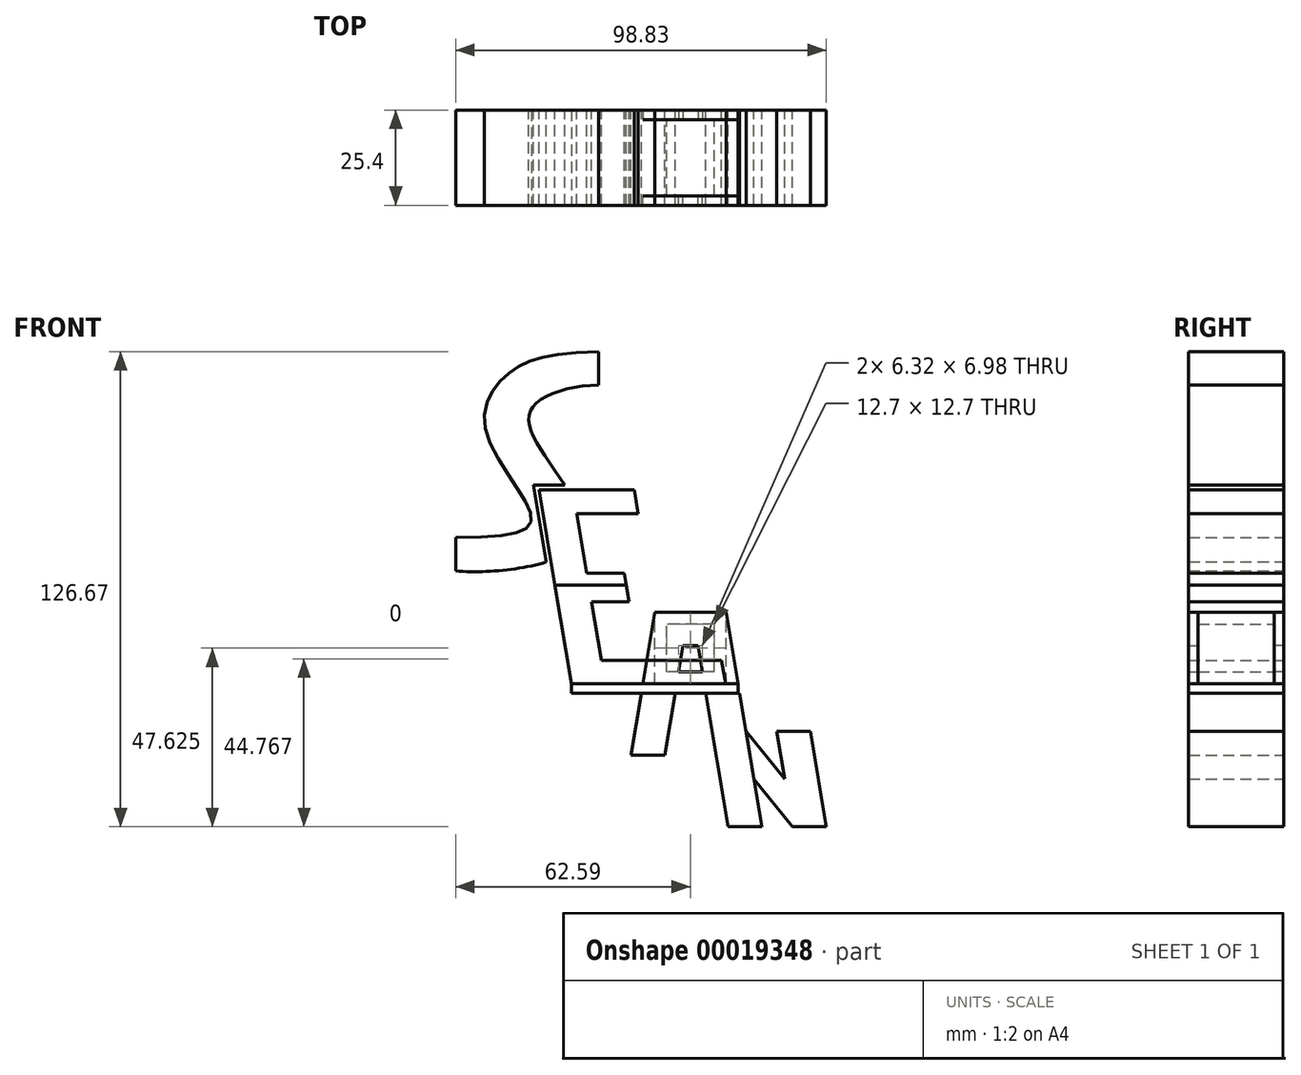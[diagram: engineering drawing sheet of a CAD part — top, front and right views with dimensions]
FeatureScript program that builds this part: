
annotation { "Feature Type Name" : "Feature", "Feature Type Description" : "" }
export const myFeature = defineFeature(function(context is Context, id is Id, definition is map)
    precondition{}
    {
        {
            var Q0;
            Q0=qCreatedBy(makeId("Top.planeOp"),FACE);
            var sketch = newSketch(context, id + "F0", { "sketchPlane" : qUnion([Q0])});
            skLineSegment(sketch, "E0.bottom", {"start": v(-44.45, 12.7) * mm, "end": v(0, 12.7) * mm});
            skLineSegment(sketch, "E0.top", {"start": v(-44.45, -12.7) * mm, "end": v(0, -12.7) * mm});
            skLineSegment(sketch, "E0.left", {"start": v(-44.45, 12.7) * mm, "end": v(-44.45, -12.7) * mm});
            skLineSegment(sketch, "E0.right", {"start": v(0, 12.7) * mm, "end": v(0, -12.7) * mm});
            skSolve(sketch);
        }
        {
            var Q0;
            Q0=makeQuery(id+"F0.imprint","IMPRINT",FACE,{"disambiguationData":[TD([[makeQuery(id+"F0.imprint","IMPRINT",EDGE,{"derivedFrom":sQuery(id+"F0.wireOp",EDGE,"E0.bottom")}),-1.0]])]});
            extrude(context, id + "F1", {"entities" : qUnion([Q0]), "depth" : 2.54 * mm});
        }
        {
            var Q0;
            Q0=qCreatedBy(makeId("Front.planeOp"),FACE);
            var sketch = newSketch(context, id + "F2", { "sketchPlane" : qUnion([Q0])});
            skPoint(sketch, "E1.0", {"position": v(0, 2.54) * mm});
            skLineSegment(sketch, "E2.bottom", {"start": v(-3.18, 2.54) * mm, "end": v(-22.22, 2.54) * mm});
            skLineSegment(sketch, "E2.top", {"start": v(-3.18, 21.6) * mm, "end": v(-22.22, 21.6) * mm});
            skLineSegment(sketch, "E2.left", {"start": v(-3.18, 2.54) * mm, "end": v(-3.18, 21.6) * mm});
            skLineSegment(sketch, "E2.right", {"start": v(-22.22, 2.54) * mm, "end": v(-22.22, 21.6) * mm});
            skLineSegment(sketch, "E3.0", {"start": v(-19.05, 5.72) * mm, "end": v(-19.05, 18.42) * mm});
            skLineSegment(sketch, "E3.1", {"start": v(-6.35, 5.72) * mm, "end": v(-19.05, 5.72) * mm});
            skLineSegment(sketch, "E3.2", {"start": v(-6.35, 5.72) * mm, "end": v(-6.35, 18.42) * mm});
            skLineSegment(sketch, "E3.3", {"start": v(-6.35, 18.42) * mm, "end": v(-19.05, 18.42) * mm});
            skSolve(sketch);
        }
        {
            var Q0;
            Q0=makeQuery(id+"F2.imprint","IMPRINT",FACE,{"disambiguationData":[TD([[makeQuery(id+"F2.imprint","IMPRINT",EDGE,{"derivedFrom":sQuery(id+"F2.wireOp",EDGE,"E2.bottom")}),-1.0]])]});
            extrude(context, id + "F3", {"entities" : qUnion([Q0]), "endBound" : BoundingType.SYMMETRIC, "depth" : 20.32 * mm});
        }
        {
            var Q0;
            Q0=makeQuery(id+"F3.opExtrude","CAP_FACE",FACE,{"disambiguationData":[OSD([sQuery(id+"F2.wireOp",EDGE,"E2.bottom"),sQuery(id+"F2.wireOp",EDGE,"E2.top"),sQuery(id+"F2.wireOp",EDGE,"E2.left"),sQuery(id+"F2.wireOp",EDGE,"E2.right"),sQuery(id+"F2.wireOp",EDGE,"E3.0"),sQuery(id+"F2.wireOp",EDGE,"E3.1"),sQuery(id+"F2.wireOp",EDGE,"E3.2"),sQuery(id+"F2.wireOp",EDGE,"E3.3")])],"isStart":false});
            var sketch = newSketch(context, id + "F4", { "sketchPlane" : qUnion([Q0])});
            skPoint(sketch, "E4.0", {"position": v(0, 2.54) * mm});
            skLineSegment(sketch, "E5", {"start": v(0, 2.54) * mm, "end": v(-3.18, 21.6) * mm});
            skLineSegment(sketch, "E6", {"start": v(-3.18, 21.6) * mm, "end": v(-22.22, 21.6) * mm});
            skLineSegment(sketch, "E7", {"start": v(-22.22, 21.6) * mm, "end": v(-25.4, 2.54) * mm});
            skLineSegment(sketch, "E8", {"start": v(-25.4, 2.54) * mm, "end": v(0, 2.54) * mm});
            skLineSegment(sketch, "E9.0", {"start": v(-14.7, 12.7) * mm, "end": v(-15.86, 5.72) * mm});
            skLineSegment(sketch, "E9.1", {"start": v(-10.7, 12.7) * mm, "end": v(-14.7, 12.7) * mm});
            skLineSegment(sketch, "E9.2", {"start": v(-9.54, 5.72) * mm, "end": v(-10.7, 12.7) * mm});
            skLineSegment(sketch, "E9.3", {"start": v(-15.86, 5.72) * mm, "end": v(-9.54, 5.72) * mm});
            skLineSegment(sketch, "E10.0", {"start": v(-9.54, 5.72) * mm, "end": v(-15.86, 5.72) * mm});
            skPoint(sketch, "E11.orphan", {"position": v(-19.05, 5.72) * mm});
            skPoint(sketch, "E12.orphan", {"position": v(-6.35, 5.72) * mm});
            skSolve(sketch);
        }
        {
            var Q0;
            Q0 = qSketchRegion(id + "F4", true);
            var Q1;
            Q1=makeQuery(id+"F1.opExtrude","SWEPT_FACE",FACE,{"disambiguationData":[OSD([sQuery(id+"F0.wireOp",EDGE,"E0.top")])]});
            var Q2;
            Q2=makeQuery(id+"F1.opExtrude","SWEPT_BODY",BODY,{"disambiguationData":[OSD([sQuery(id+"F0.wireOp",EDGE,"E0.bottom"),sQuery(id+"F0.wireOp",EDGE,"E0.top"),sQuery(id+"F0.wireOp",EDGE,"E0.left"),sQuery(id+"F0.wireOp",EDGE,"E0.right")])]});
            extrude(context, id + "F5", {"entities" : qUnion([Q0]), "endBound" : BoundingType.UP_TO_SURFACE, "endBoundEntityFace" : qUnion([Q1]), "endBoundEntityBody" : qUnion([Q2]), "depth" : 25.4 * mm});
        }
        {
            var Q0;
            Q0=makeQuery(id+"F5.opExtrude","SWEPT_BODY",BODY,{"disambiguationData":[OSD([sQuery(id+"F4.wireOp",EDGE,"E5"),sQuery(id+"F4.wireOp",EDGE,"E6"),sQuery(id+"F4.wireOp",EDGE,"E7"),sQuery(id+"F4.wireOp",EDGE,"E8"),sQuery(id+"F4.wireOp",EDGE,"E9.0"),sQuery(id+"F4.wireOp",EDGE,"E9.1"),sQuery(id+"F4.wireOp",EDGE,"E9.2"),sQuery(id+"F4.wireOp",EDGE,"E10.0")])]});
            var Q1;
            Q1=qCreatedBy(makeId("Front.planeOp"),FACE);
            mirror(context, id + "F6", {"entities" : qUnion([Q0]), "mirrorPlane" : qUnion([Q1])});
        }
        {
            var Q0;
            Q0=qCreatedBy(makeId("Front.planeOp"),FACE);
            var sketch = newSketch(context, id + "F7", { "sketchPlane" : qUnion([Q0])});
            skPoint(sketch, "E13.0", {"position": v(-44.45, 2.54) * mm});
            skLineSegment(sketch, "E14", {"start": v(-44.45, 2.54) * mm, "end": v(-3.34, 2.54) * mm});
            skPoint(sketch, "E15.0", {"position": v(-22.22, 21.6) * mm});
            skLineSegment(sketch, "E16", {"start": v(-44.45, 2.54) * mm, "end": v(-48.83, 28.85) * mm});
            skLineSegment(sketch, "E17", {"start": v(-48.83, 28.85) * mm, "end": v(-29.78, 28.85) * mm});
            skLineSegment(sketch, "E18.0", {"start": v(-39.1, 24.46) * mm, "end": v(-29.05, 24.46) * mm});
            skLineSegment(sketch, "E18.1", {"start": v(-36.48, 8.8) * mm, "end": v(-39.1, 24.46) * mm});
            skLineSegment(sketch, "E18.2", {"start": v(-36.48, 8.8) * mm, "end": v(-4.38, 8.8) * mm});
            skLineSegment(sketch, "E19", {"start": v(-29.78, 28.85) * mm, "end": v(-29.05, 24.46) * mm});
            skLineSegment(sketch, "E20", {"start": v(-4.38, 8.8) * mm, "end": v(-3.34, 2.54) * mm});
            skSolve(sketch);
        }
        {
            var Q0;
            Q0=makeQuery(id+"F7.imprint","IMPRINT",FACE,{"disambiguationData":[TD([[makeQuery(id+"F7.imprint","IMPRINT",EDGE,{"derivedFrom":sQuery(id+"F7.wireOp",EDGE,"E14")}),1.0]])]});
            extrude(context, id + "F8", {"entities" : qUnion([Q0]), "endBound" : BoundingType.SYMMETRIC, "depth" : 25.4 * mm});
        }
        {
            var Q0;
            Q0=qCreatedBy(makeId("Front.planeOp"),FACE);
            var sketch = newSketch(context, id + "F9", { "sketchPlane" : qUnion([Q0])});
            skPoint(sketch, "E21.0", {"position": v(-48.83, 28.85) * mm});
            skPoint(sketch, "E22.0", {"position": v(-29.78, 28.85) * mm});
            skLineSegment(sketch, "E23", {"start": v(-48.83, 28.85) * mm, "end": v(-29.78, 28.85) * mm});
            skLineSegment(sketch, "E24", {"start": v(-48.83, 28.85) * mm, "end": v(-53.07, 54.25) * mm});
            skLineSegment(sketch, "E25", {"start": v(-53.07, 54.25) * mm, "end": v(-27.67, 54.25) * mm});
            skLineSegment(sketch, "E26.0", {"start": v(-43, 47.9) * mm, "end": v(-26.6, 47.9) * mm});
            skLineSegment(sketch, "E26.1", {"start": v(-40.34, 31.98) * mm, "end": v(-43, 47.9) * mm});
            skLineSegment(sketch, "E26.2", {"start": v(-40.34, 31.98) * mm, "end": v(-30.3, 31.98) * mm});
            skLineSegment(sketch, "E27", {"start": v(-27.67, 54.25) * mm, "end": v(-26.6, 47.9) * mm});
            skLineSegment(sketch, "E28", {"start": v(-30.3, 31.98) * mm, "end": v(-29.78, 28.85) * mm});
            skSolve(sketch);
        }
        {
            var Q0;
            Q0 = qSketchRegion(id + "F9", true);
            extrude(context, id + "F10", {"entities" : qUnion([Q0]), "endBound" : BoundingType.SYMMETRIC, "depth" : 25.4 * mm});
        }
        {
            var Q0;
            Q0=qCreatedBy(makeId("Front.planeOp"),FACE);
            var sketch = newSketch(context, id + "F11", { "sketchPlane" : qUnion([Q0])});
            skLineSegment(sketch, "E29.0", {"start": v(-25.4, 2.54) * mm, "end": v(-22.22, 21.6) * mm});
            skLineSegment(sketch, "E29.1", {"start": v(-14.7, 12.7) * mm, "end": v(-14.7, 12.7) * mm});
            skLineSegment(sketch, "E29.2", {"start": v(-10.7, 12.7) * mm, "end": v(-10.7, 12.7) * mm});
            skLineSegment(sketch, "E29.3", {"start": v(-3.18, 21.6) * mm, "end": v(0, 2.54) * mm});
            skLineSegment(sketch, "E30", {"start": v(-25.82, 0) * mm, "end": v(-28.58, -16.5) * mm});
            skLineSegment(sketch, "E31", {"start": v(-16.81, 0) * mm, "end": v(-19.56, -16.5) * mm});
            skLineSegment(sketch, "E32", {"start": v(-19.56, -16.5) * mm, "end": v(-28.58, -16.51) * mm});
            skLineSegment(sketch, "E33", {"start": v(-8.59, 0) * mm, "end": v(-2.66, -35.56) * mm});
            skLineSegment(sketch, "E34", {"start": v(0.42, 0) * mm, "end": v(6.35, -35.56) * mm});
            skLineSegment(sketch, "E35", {"start": v(6.35, -35.56) * mm, "end": v(-2.66, -35.56) * mm});
            skLineSegment(sketch, "E36.0", {"start": v(-25.82, 0) * mm, "end": v(-16.81, 0) * mm});
            skPoint(sketch, "E37.orphan", {"position": v(-44.45, 0) * mm});
            skLineSegment(sketch, "E38.trimOffspring", {"start": v(-8.59, 0) * mm, "end": v(0, 0) * mm});
            skLineSegment(sketch, "E39", {"start": v(0, 0) * mm, "end": v(0.42, 0) * mm});
            skSolve(sketch);
        }
        {
            var Q0;
            Q0=makeQuery(id+"F11.imprint","IMPRINT",FACE,{"disambiguationData":[TD([[makeQuery(id+"F11.imprint","IMPRINT",EDGE,{"derivedFrom":sQuery(id+"F11.wireOp",EDGE,"E30")}),1.0]])]});
            var Q1;
            Q1=makeQuery(id+"F11.imprint","IMPRINT",FACE,{"disambiguationData":[TD([[makeQuery(id+"F11.imprint","IMPRINT",EDGE,{"derivedFrom":sQuery(id+"F11.wireOp",EDGE,"E33")}),1.0]])]});
            extrude(context, id + "F12", {"entities" : qUnion([Q0, Q1]), "endBound" : BoundingType.SYMMETRIC, "depth" : 25.4 * mm});
        }
        {
            var Q0;
            Q0=qCreatedBy(makeId("Front.planeOp"),FACE);
            var sketch = newSketch(context, id + "F13", { "sketchPlane" : qUnion([Q0])});
            skPoint(sketch, "E40.0", {"position": v(-19.56, -16.5) * mm});
            skLineSegment(sketch, "E41.0", {"start": v(0.42, 0) * mm, "end": v(6.35, -35.56) * mm});
            skLineSegment(sketch, "E42", {"start": v(2.12, -10.16) * mm, "end": v(12.4, -22.86) * mm});
            skLineSegment(sketch, "E43", {"start": v(12.4, -22.86) * mm, "end": v(10.29, -10.16) * mm});
            skLineSegment(sketch, "E44", {"start": v(10.29, -10.16) * mm, "end": v(19.3, -10.16) * mm});
            skLineSegment(sketch, "E45", {"start": v(19.3, -10.16) * mm, "end": v(23.54, -35.56) * mm});
            skLineSegment(sketch, "E46", {"start": v(23.54, -35.56) * mm, "end": v(14.52, -35.56) * mm});
            skLineSegment(sketch, "E47", {"start": v(14.52, -35.56) * mm, "end": v(4.23, -22.86) * mm});
            skSolve(sketch);
        }
        {
            var Q0;
            {var subQ1=sQuery(id+"F13.wireOp",EDGE,"E42");Q0=makeQuery(id+"F13.imprint","IMPRINT",FACE,{"disambiguationData":[TD([[makeQuery(id+"F13.imprint","IMPRINT",EDGE,{"derivedFrom":subQ1}),-1.0]])]});}
            extrude(context, id + "F14", {"entities" : qUnion([Q0]), "endBound" : BoundingType.SYMMETRIC, "depth" : 25.4 * mm});
        }
        {
            var Q0;
            Q0=qCreatedBy(makeId("Front.planeOp"),FACE);
            var sketch = newSketch(context, id + "F15", { "sketchPlane" : qUnion([Q0])});
            skFitSpline(sketch, "E48", {"points": [v(-75.3, 32.6) * mm, v(-41.98, 41.06) * mm, v(-51.6, 63.35) * mm, v(-55, 76) * mm, v(-37.2, 82.22) * mm], "startDerivative": vector(108.9, -8.28) * mm, "endDerivative": vector(96.18, 1.7) * mm});
            skLineSegment(sketch, "E49", {"start": v(-75.3, 32.6) * mm, "end": v(-75.3, 41.5) * mm});
            skLineSegment(sketch, "E50", {"start": v(-37.2, 82.22) * mm, "end": v(-37.2, 91.11) * mm});
            skFitSpline(sketch, "E51", {"points": [v(-75.3, 41.5) * mm, v(-55.18, 47.17) * mm, v(-67.4, 70.33) * mm, v(-61.47, 85.06) * mm, v(-37.2, 91.11) * mm], "startDerivative": vector(172.35, 1.86) * mm, "endDerivative": vector(150.59, 5.63) * mm});
            skLineSegment(sketch, "E52.0", {"start": v(-53.07, 54.25) * mm, "end": v(-27.67, 54.25) * mm});
            skPoint(sketch, "E53", {"position": v(-40.37, 54.25) * mm});
            skLineSegment(sketch, "E54.0", {"start": v(-54.57, 55.52) * mm, "end": v(-27.67, 55.52) * mm});
            skLineSegment(sketch, "E54.1", {"start": v(-50.09, 28.64) * mm, "end": v(-54.57, 55.52) * mm});
            skSolve(sketch);
        }
        {
            var Q0;
            {var subQ7=sQuery(id+"F15.wireOp",EDGE,"E49");Q0=makeQuery(id+"F15.imprint","IMPRINT",FACE,{"disambiguationData":[TD([[makeQuery(id+"F15.imprint","IMPRINT",EDGE,{"derivedFrom":subQ7}),-1.0]])]});}
            extrude(context, id + "F16", {"entities" : qUnion([Q0]), "endBound" : BoundingType.SYMMETRIC, "depth" : 25.4 * mm});
        }
    });
